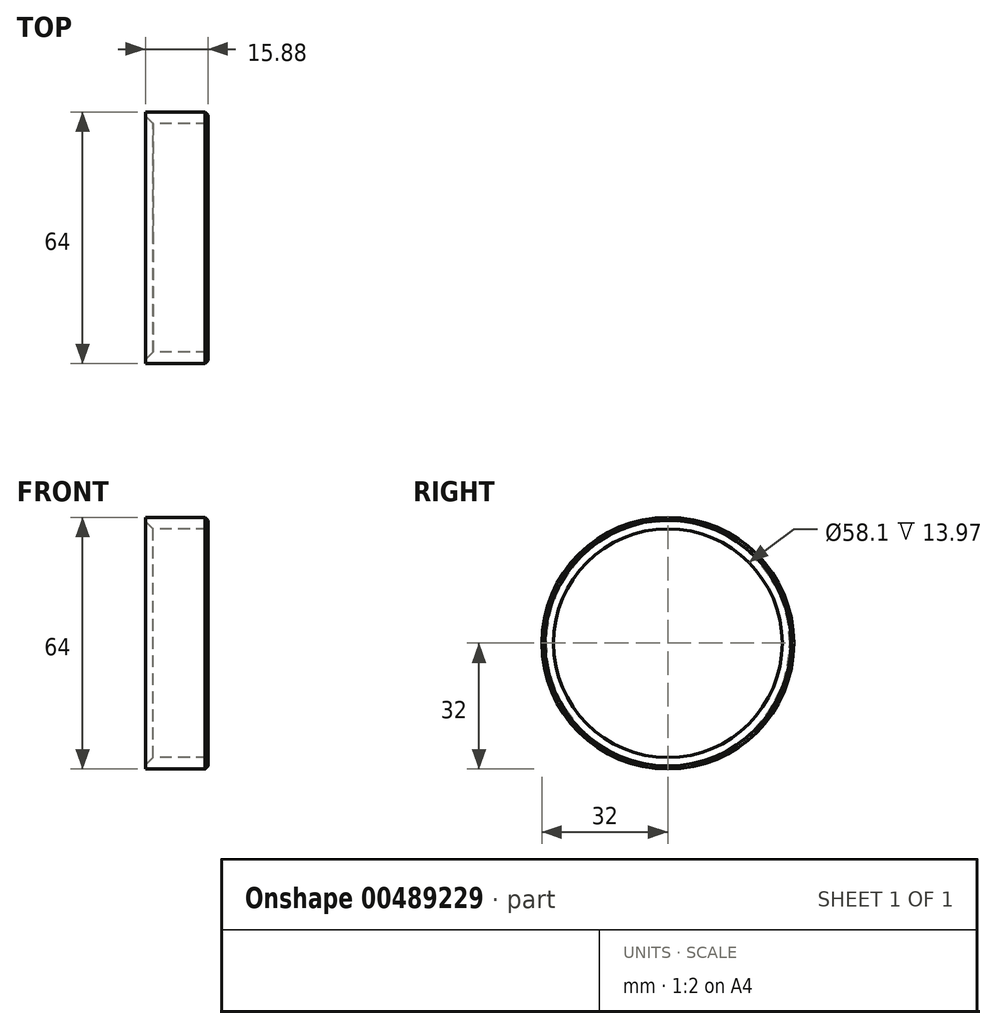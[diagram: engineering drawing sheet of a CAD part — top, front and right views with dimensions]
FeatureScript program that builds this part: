
annotation { "Feature Type Name" : "Feature", "Feature Type Description" : "" }
export const myFeature = defineFeature(function(context is Context, id is Id, definition is map)
    precondition{}
    {
        {
            var Q0;
            Q0=qCreatedBy(makeId("Right.planeOp"),FACE);
            var sketch = newSketch(context, id + "F0", { "sketchPlane" : qUnion([Q0])});
            skCircle(sketch, "E0", {"center": v(0, 0) * mm, "radius": 29.05 * mm});
            skCircle(sketch, "E1", {"center": v(0, 0) * mm, "radius": 32 * mm});
            skSolve(sketch);
        }
        {
            var Q0;
            Q0 = qSketchRegion(id + "F0", true);
            extrude(context, id + "F1", {"entities" : qUnion([Q0]), "depth" : 15.88 * mm});
        }
        {
            var Q0;
            Q0=makeQuery(id+"F1.opExtrude","CAP_EDGE",EDGE,{"disambiguationData":[OSD([sQuery(id+"F0.wireOp",EDGE,"E0")])],"isStart":true});
            chamfer(context, id + "F2", {"entities" : qUnion([Q0]), "width" : 1.9 * mm, "tangentPropagation" : true});
        }
        {
            var Q0;
            Q0=makeQuery(id+"F1.opExtrude","CAP_EDGE",EDGE,{"disambiguationData":[OSD([sQuery(id+"F0.wireOp",EDGE,"E1")])],"isStart":false});
            chamfer(context, id + "F3", {"entities" : qUnion([Q0]), "width" : 0.76 * mm, "tangentPropagation" : true});
        }
    });
